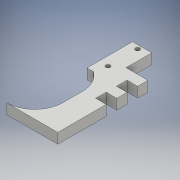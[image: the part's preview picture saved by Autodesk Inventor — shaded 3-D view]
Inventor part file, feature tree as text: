
AUTODESK INVENTOR PART (.ipt)
format: ipt  version: 2017 (Build 210142000, 142)  size: 141,312 bytes
history: native  units: mm
features: sketch x2, extrude x1, hole x1
ambient origin geometry x8: Origin, YZ Plane, XZ Plane, XY Plane, X Axis, Y Axis, Z Axis, Center Point
bodies: Body1 (feature_tree)
feature tree (4):
  extrude  "Extrusion2"  TaperAngle=90.0deg  [1 undecoded]
  hole  "Hole2"  [1 undecoded]
  sketch  "Sketch1"  dims[d0=22.0mm d1=90.0deg]
  sketch  "Sketch5"  dims[d2=0.0mm d3=15.0mm d4=0.0mm d5=13.0mm d6=22.0mm d7=0.0mm d9=15.0mm d14=8.2mm d15=8.2mm d17=7.5mm d32=8.0mm d34=8.0mm d35=8.0mm d37=15.0mm d39=40.0mm d40=0.0mm d41=0.0mm d42=20.0mm d43=8.2mm d44=90.0mm d45=8.0mm d46=0.0mm d47=23.0mm d48=3.0mm d49=0.0mm d51=3.4mm d52=6.0mm d53=4.0mm d54=2.0mm d55=90.0deg d56=8.0mm d57=20.594885mm d58=15.0mm]
note: 2 required parameter values undecoded (feature->parameter linkage not recoverable at this tier; creation-order binding heuristic only, values carry confidence <= 0.55)
